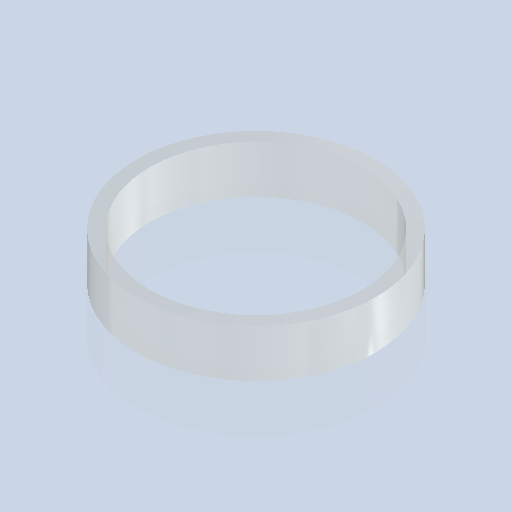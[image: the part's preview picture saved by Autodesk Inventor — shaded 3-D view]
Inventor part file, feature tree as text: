
AUTODESK INVENTOR PART (.ipt)
format: ipt  version: 2024.2 (Build 282272000, 272)  size: 242,688 bytes
history: native  units: mm
features: extrude x2, sketch x2
ambient origin geometry x8: Origin, YZ Plane, XZ Plane, XY Plane, X Axis, Y Axis, Z Axis, Center Point
bodies: Volumenkörper1 (feature_tree)
feature tree (4):
  extrude  "Extrusion1"  Depth=18.0mm TaperAngle=0.0deg
  extrude  "Extrusion2"  Depth=18.0mm TaperAngle=0.0deg
  sketch  "Skizze1"  dims[d0=90.0mm d1=18.0mm d2=0.0mm]
  sketch  "Skizze2"  dims[d3=80.0mm d4=18.0mm d5=0.0mm]
